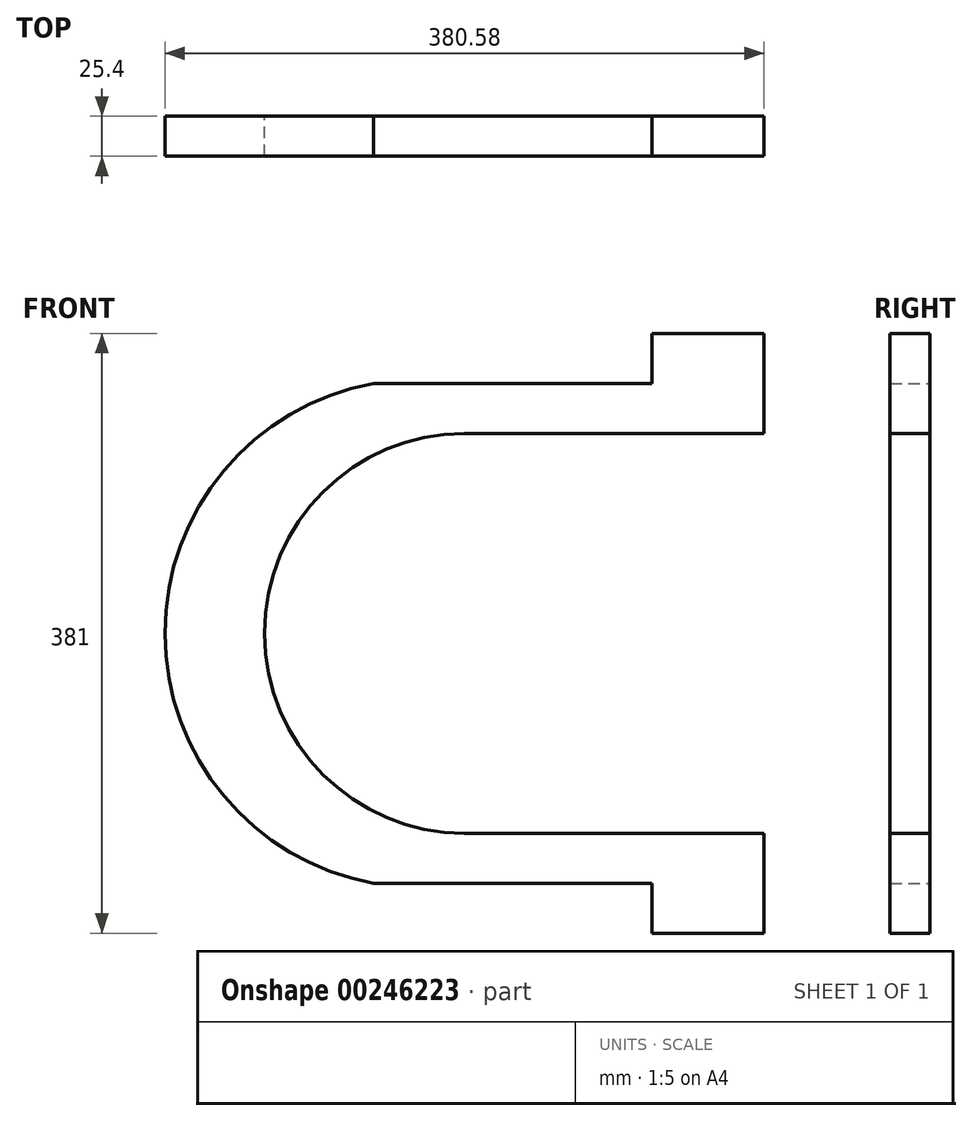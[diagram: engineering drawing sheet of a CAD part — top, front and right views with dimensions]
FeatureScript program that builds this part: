
annotation { "Feature Type Name" : "Feature", "Feature Type Description" : "" }
export const myFeature = defineFeature(function(context is Context, id is Id, definition is map)
    precondition{}
    {
        {
            var Q0;
            Q0=qCreatedBy(makeId("Front.planeOp"),FACE);
            var sketch = newSketch(context, id + "F0", { "sketchPlane" : qUnion([Q0])});
            skLineSegment(sketch, "E0.bottom", {"start": v(190.3, 158.75) * mm, "end": v(185.23, 158.75) * mm});
            skLineSegment(sketch, "E0.top", {"start": v(119.17, -158.75) * mm, "end": v(-57.85, -158.75) * mm});
            skLineSegment(sketch, "E0.left", {"start": v(190.3, 158.75) * mm, "end": v(190.3, 127) * mm});
            skPoint(sketch, "E0.middle", {"position": v(0, 0) * mm});
            skArc(sketch, "E1", {"start": v(0, 127) * mm, "mid": v(-127, 0) * mm, "end": v(0, -127) * mm});
            skLineSegment(sketch, "E2", {"start": v(0, 127) * mm, "end": v(153.1, 127) * mm});
            skLineSegment(sketch, "E3", {"start": v(0, -127) * mm, "end": v(190.3, -127) * mm});
            skPoint(sketch, "E4.orphan", {"position": v(190.3, 0) * mm});
            skLineSegment(sketch, "E5.trimOffspring", {"start": v(190.3, -127) * mm, "end": v(190.3, -158.75) * mm});
            skLineSegment(sketch, "E6.bottom", {"start": v(153.1, 127) * mm, "end": v(190.3, 127) * mm});
            skPoint(sketch, "E6.middle", {"position": v(185.23, 158.75) * mm});
            skPoint(sketch, "E6.top.end.orphan", {"position": v(217.37, 190.5) * mm});
            skPoint(sketch, "E6.top.start.orphan", {"position": v(158.39, 190.5) * mm});
            skPoint(sketch, "E7.orphan", {"position": v(212.07, 127) * mm});
            skLineSegment(sketch, "E8.top", {"start": v(190.3, 190.5) * mm, "end": v(119.17, 190.5) * mm});
            skLineSegment(sketch, "E8.left", {"start": v(190.3, 158.75) * mm, "end": v(190.3, 190.5) * mm});
            skLineSegment(sketch, "E8.right", {"start": v(119.17, 158.75) * mm, "end": v(119.17, 190.5) * mm});
            skLineSegment(sketch, "E9.left", {"start": v(190.3, -158.75) * mm, "end": v(190.3, -158.75) * mm});
            skLineSegment(sketch, "E9.right", {"start": v(119.17, -158.75) * mm, "end": v(119.17, -158.75) * mm});
            skLineSegment(sketch, "E10.top", {"start": v(190.3, -190.5) * mm, "end": v(119.17, -190.5) * mm});
            skLineSegment(sketch, "E10.left", {"start": v(190.3, -158.75) * mm, "end": v(190.3, -190.5) * mm});
            skArc(sketch, "E11", {"start": v(-57.85, 158.75) * mm, "mid": v(-190.3, 0) * mm, "end": v(-57.85, -158.75) * mm});
            skPoint(sketch, "E12.orphan", {"position": v(-190.3, -158.75) * mm});
            skPoint(sketch, "E13.orphan", {"position": v(-190.3, 158.75) * mm});
            skLineSegment(sketch, "E14.trimOffspring", {"start": v(119.17, 158.75) * mm, "end": v(-57.85, 158.75) * mm});
            skPoint(sketch, "E15.orphan", {"position": v(0, -158.75) * mm});
            skPoint(sketch, "E16.orphan", {"position": v(0, 158.75) * mm});
            skLineSegment(sketch, "E17", {"start": v(119.17, -158.75) * mm, "end": v(119.17, -190.5) * mm});
            skPoint(sketch, "E18.trimOffspring.end.orphan", {"position": v(-190.3, 0) * mm});
            skSolve(sketch);
        }
        {
            var Q0;
            Q0=makeQuery(id+"F0.imprint","IMPRINT",FACE,{"disambiguationData":[TD([[makeQuery(id+"F0.imprint","IMPRINT",EDGE,{"derivedFrom":sQuery(id+"F0.wireOp",EDGE,"E0.top")}),-1.0]])]});
            extrude(context, id + "F1", {"entities" : qUnion([Q0]), "depth" : 25.4 * mm});
        }
    });
